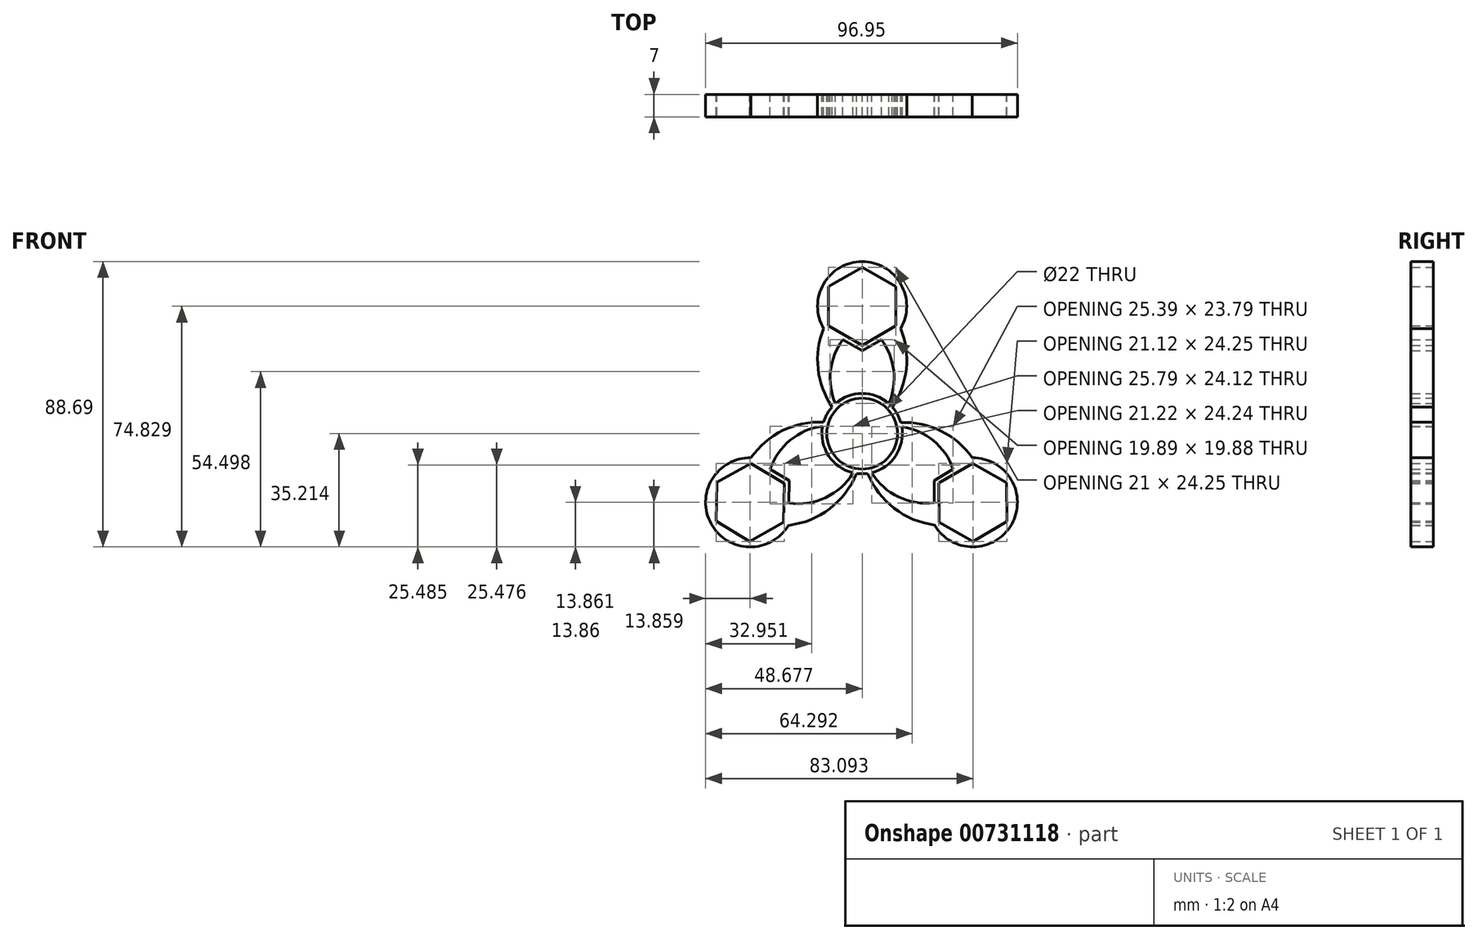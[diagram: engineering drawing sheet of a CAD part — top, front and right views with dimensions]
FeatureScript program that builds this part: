
annotation { "Feature Type Name" : "Feature", "Feature Type Description" : "" }
export const myFeature = defineFeature(function(context is Context, id is Id, definition is map)
    precondition{}
    {
        {
            var Q0;
            Q0=qCreatedBy(makeId("Front.planeOp"),FACE);
            var sketch = newSketch(context, id + "F0", { "sketchPlane" : qUnion([Q0])});
            skCircle(sketch, "E0", {"center": v(-1.02, 1.88) * mm, "radius": 11 * mm});
            skCircle(sketch, "E1", {"center": v(-1.02, 1.88) * mm, "radius": 12.5 * mm});
            skCircle(sketch, "E2.cCircle", {"center": v(-1.02, 41.5) * mm, "radius": 10.5 * mm, "construction": true});
            skLineSegment(sketch, "E2.0", {"start": v(9.48, 47.56) * mm, "end": v(9.48, 35.44) * mm});
            skLineSegment(sketch, "E2.1", {"start": v(9.48, 35.44) * mm, "end": v(-1.02, 29.37) * mm});
            skLineSegment(sketch, "E2.2", {"start": v(-1.02, 29.37) * mm, "end": v(-11.52, 35.44) * mm});
            skLineSegment(sketch, "E2.3", {"start": v(-11.52, 35.44) * mm, "end": v(-11.52, 47.56) * mm});
            skLineSegment(sketch, "E2.4", {"start": v(-11.52, 47.56) * mm, "end": v(-1.02, 53.62) * mm});
            skLineSegment(sketch, "E2.5", {"start": v(-1.02, 53.62) * mm, "end": v(9.48, 47.56) * mm});
            skPoint(sketch, "E2.0.midPoint", {"position": v(9.48, 41.5) * mm});
            skCircle(sketch, "E3.cCircle", {"center": v(-35.84, -19.47) * mm, "radius": 10.5 * mm, "construction": true});
            skLineSegment(sketch, "E3.0", {"start": v(-25.23, -13.6) * mm, "end": v(-25.45, -25.73) * mm});
            skLineSegment(sketch, "E3.1", {"start": v(-25.45, -25.73) * mm, "end": v(-36.07, -31.6) * mm});
            skLineSegment(sketch, "E3.2", {"start": v(-36.07, -31.6) * mm, "end": v(-46.45, -25.33) * mm});
            skLineSegment(sketch, "E3.3", {"start": v(-46.45, -25.33) * mm, "end": v(-46.22, -13.21) * mm});
            skLineSegment(sketch, "E3.4", {"start": v(-46.22, -13.21) * mm, "end": v(-35.61, -7.35) * mm});
            skLineSegment(sketch, "E3.5", {"start": v(-35.61, -7.35) * mm, "end": v(-25.23, -13.6) * mm});
            skPoint(sketch, "E3.0.midPoint", {"position": v(-25.34, -19.67) * mm});
            skCircle(sketch, "E4.cCircle", {"center": v(33.4, -19.47) * mm, "radius": 10.5 * mm, "construction": true});
            skLineSegment(sketch, "E4.0", {"start": v(33.52, -31.6) * mm, "end": v(22.95, -25.64) * mm});
            skLineSegment(sketch, "E4.1", {"start": v(22.95, -25.64) * mm, "end": v(22.83, -13.52) * mm});
            skLineSegment(sketch, "E4.2", {"start": v(22.83, -13.52) * mm, "end": v(33.27, -7.35) * mm});
            skLineSegment(sketch, "E4.3", {"start": v(33.27, -7.35) * mm, "end": v(43.83, -13.3) * mm});
            skLineSegment(sketch, "E4.4", {"start": v(43.83, -13.3) * mm, "end": v(43.95, -25.43) * mm});
            skLineSegment(sketch, "E4.5", {"start": v(43.95, -25.43) * mm, "end": v(33.52, -31.6) * mm});
            skPoint(sketch, "E4.0.midPoint", {"position": v(28.23, -28.62) * mm});
            skCircle(sketch, "E5.cCircle", {"center": v(-1.02, 41.5) * mm, "radius": 12 * mm, "construction": true});
            skLineSegment(sketch, "E5.0", {"start": v(10.98, 48.43) * mm, "end": v(10.98, 34.57) * mm});
            skLineSegment(sketch, "E5.1", {"start": v(10.98, 34.57) * mm, "end": v(-1.02, 27.64) * mm});
            skLineSegment(sketch, "E5.2", {"start": v(-1.02, 27.64) * mm, "end": v(-13.02, 34.57) * mm});
            skLineSegment(sketch, "E5.3", {"start": v(-13.02, 34.57) * mm, "end": v(-13.02, 48.43) * mm});
            skLineSegment(sketch, "E5.4", {"start": v(-13.02, 48.43) * mm, "end": v(-1.02, 55.36) * mm});
            skLineSegment(sketch, "E5.5", {"start": v(-1.02, 55.36) * mm, "end": v(10.98, 48.43) * mm});
            skPoint(sketch, "E5.0.midPoint", {"position": v(10.98, 41.5) * mm});
            skCircle(sketch, "E6.cCircle", {"center": v(33.4, -19.47) * mm, "radius": 12 * mm, "construction": true});
            skLineSegment(sketch, "E6.0", {"start": v(33.25, -5.62) * mm, "end": v(45.32, -12.42) * mm});
            skLineSegment(sketch, "E6.1", {"start": v(45.32, -12.42) * mm, "end": v(45.46, -26.27) * mm});
            skLineSegment(sketch, "E6.2", {"start": v(45.46, -26.27) * mm, "end": v(33.54, -33.33) * mm});
            skLineSegment(sketch, "E6.3", {"start": v(33.54, -33.33) * mm, "end": v(21.47, -26.52) * mm});
            skLineSegment(sketch, "E6.4", {"start": v(21.47, -26.52) * mm, "end": v(21.32, -12.67) * mm});
            skLineSegment(sketch, "E6.5", {"start": v(21.32, -12.67) * mm, "end": v(33.25, -5.62) * mm});
            skPoint(sketch, "E6.0.midPoint", {"position": v(39.28, -9.02) * mm});
            skCircle(sketch, "E7.cCircle", {"center": v(-35.84, -19.47) * mm, "radius": 12 * mm, "construction": true});
            skLineSegment(sketch, "E7.0", {"start": v(-35.58, -5.62) * mm, "end": v(-23.71, -12.77) * mm});
            skLineSegment(sketch, "E7.1", {"start": v(-23.71, -12.77) * mm, "end": v(-23.97, -26.62) * mm});
            skLineSegment(sketch, "E7.2", {"start": v(-23.97, -26.62) * mm, "end": v(-36.1, -33.32) * mm});
            skLineSegment(sketch, "E7.3", {"start": v(-36.1, -33.32) * mm, "end": v(-47.97, -26.17) * mm});
            skLineSegment(sketch, "E7.4", {"start": v(-47.97, -26.17) * mm, "end": v(-47.7, -12.32) * mm});
            skLineSegment(sketch, "E7.5", {"start": v(-47.7, -12.32) * mm, "end": v(-35.58, -5.62) * mm});
            skPoint(sketch, "E7.0.midPoint", {"position": v(-29.65, -9.2) * mm});
            skPoint(sketch, "E8.startSnap0", {"position": v(27.5, -29.93) * mm});
            skArc(sketch, "E9", {"start": v(-1.02, 1.88) * mm, "mid": v(8.52, 15.15) * mm, "end": v(4.98, 31.1) * mm});
            skArc(sketch, "E10", {"start": v(-7.02, 31.1) * mm, "mid": v(-10.56, 15.15) * mm, "end": v(-1.02, 1.88) * mm});
            skArc(sketch, "E11", {"start": v(-1.02, 1.88) * mm, "mid": v(-17.92, 3.04) * mm, "end": v(-29.65, -9.2) * mm});
            skArc(sketch, "E12", {"start": v(-23.84, -19.7) * mm, "mid": v(-7.2, -14.44) * mm, "end": v(-1.02, 1.88) * mm});
            skArc(sketch, "E13", {"start": v(27.28, -9.14) * mm, "mid": v(15.67, 2.88) * mm, "end": v(-1.02, 1.88) * mm});
            skArc(sketch, "E14", {"start": v(-1.02, 1.88) * mm, "mid": v(5.07, -14.2) * mm, "end": v(21.4, -19.6) * mm});
            skArc(sketch, "E15", {"start": v(-23.97, -26.62) * mm, "mid": v(-6.63, -17.09) * mm, "end": v(-1.02, 1.88) * mm});
            skArc(sketch, "E16", {"start": v(-1.02, 1.88) * mm, "mid": v(-19.77, 4.91) * mm, "end": v(-35.58, -5.62) * mm});
            skArc(sketch, "E17", {"start": v(-13.02, 34.57) * mm, "mid": v(-13.3, 15.92) * mm, "end": v(-1.02, 1.88) * mm});
            skArc(sketch, "E18", {"start": v(-1.02, 1.88) * mm, "mid": v(11.26, 15.92) * mm, "end": v(10.98, 34.57) * mm});
            skArc(sketch, "E19", {"start": v(33.25, -5.62) * mm, "mid": v(17.57, 4.79) * mm, "end": v(-1.02, 1.88) * mm});
            skArc(sketch, "E20", {"start": v(-1.02, 1.88) * mm, "mid": v(4.46, -16.88) * mm, "end": v(21.47, -26.52) * mm});
            skArc(sketch, "E21", {"start": v(45.32, -12.42) * mm, "mid": v(40.2, -7.4) * mm, "end": v(33.25, -5.62) * mm});
            skArc(sketch, "E22", {"start": v(45.46, -26.27) * mm, "mid": v(47.25, -19.33) * mm, "end": v(45.32, -12.42) * mm});
            skArc(sketch, "E23", {"start": v(33.54, -33.33) * mm, "mid": v(40.45, -31.4) * mm, "end": v(45.46, -26.27) * mm});
            skArc(sketch, "E24", {"start": v(21.47, -26.52) * mm, "mid": v(26.59, -31.54) * mm, "end": v(33.54, -33.33) * mm});
            skArc(sketch, "E25", {"start": v(-36.1, -33.32) * mm, "mid": v(-29.14, -31.6) * mm, "end": v(-23.97, -26.62) * mm});
            skArc(sketch, "E26", {"start": v(-47.97, -26.17) * mm, "mid": v(-43, -31.34) * mm, "end": v(-36.1, -33.32) * mm});
            skArc(sketch, "E27", {"start": v(-47.7, -12.32) * mm, "mid": v(-49.7, -19.21) * mm, "end": v(-47.97, -26.17) * mm});
            skArc(sketch, "E28", {"start": v(-35.58, -5.62) * mm, "mid": v(-42.54, -7.34) * mm, "end": v(-47.7, -12.32) * mm});
            skArc(sketch, "E29", {"start": v(-13.02, 48.43) * mm, "mid": v(-14.88, 41.5) * mm, "end": v(-13.02, 34.57) * mm});
            skArc(sketch, "E30", {"start": v(-1.02, 55.36) * mm, "mid": v(-7.95, 53.5) * mm, "end": v(-13.02, 48.43) * mm});
            skArc(sketch, "E31", {"start": v(10.98, 48.43) * mm, "mid": v(5.9, 53.5) * mm, "end": v(-1.02, 55.36) * mm});
            skArc(sketch, "E32", {"start": v(10.98, 34.57) * mm, "mid": v(12.83, 41.5) * mm, "end": v(10.98, 48.43) * mm});
            skSolve(sketch);
        }
        {
            var Q0;
            Q0 = qSketchRegion(id + "F0", true);
            var Q1;
            {var subQ0=sQuery(id+"F0.wireOp",EDGE,"E11");var subQ1=sQuery(id+"F0.wireOp",EDGE,"E0");var subQ2=makeQuery(id+"F0.imprint","INTERSECT",VERTEX,{"derivedFrom":[subQ1,subQ0]});Q1=makeQuery(id+"F0.imprint","IMPRINT",FACE,{"disambiguationData":[TD([[makeQuery(id+"F0.imprint","IMPRINT",EDGE,{"disambiguationData":[TD([[subQ2,-1.0]])],"derivedFrom":subQ1}),-1.0]])]});}
            var Q2;
            {var subQ0=sQuery(id+"F0.wireOp",EDGE,"E9");var subQ1=sQuery(id+"F0.wireOp",EDGE,"E0");var subQ2=makeQuery(id+"F0.imprint","INTERSECT",VERTEX,{"derivedFrom":[subQ1,subQ0]});Q2=makeQuery(id+"F0.imprint","IMPRINT",FACE,{"disambiguationData":[TD([[makeQuery(id+"F0.imprint","IMPRINT",EDGE,{"disambiguationData":[TD([[subQ2,-1.0]])],"derivedFrom":subQ1}),-1.0]])]});}
            var Q3;
            {var subQ0=sQuery(id+"F0.wireOp",EDGE,"E13");var subQ1=sQuery(id+"F0.wireOp",EDGE,"E0");var subQ2=makeQuery(id+"F0.imprint","INTERSECT",VERTEX,{"derivedFrom":[subQ1,subQ0]});Q3=makeQuery(id+"F0.imprint","IMPRINT",FACE,{"disambiguationData":[TD([[makeQuery(id+"F0.imprint","IMPRINT",EDGE,{"disambiguationData":[TD([[subQ2,1.0]])],"derivedFrom":subQ1}),-1.0]])]});}
            extrude(context, id + "F1", {"entities" : qUnion([Q0, Q1, Q2, Q3]), "depth" : 7 * mm, "offsetDistance" : 25 * mm});
        }
    });
